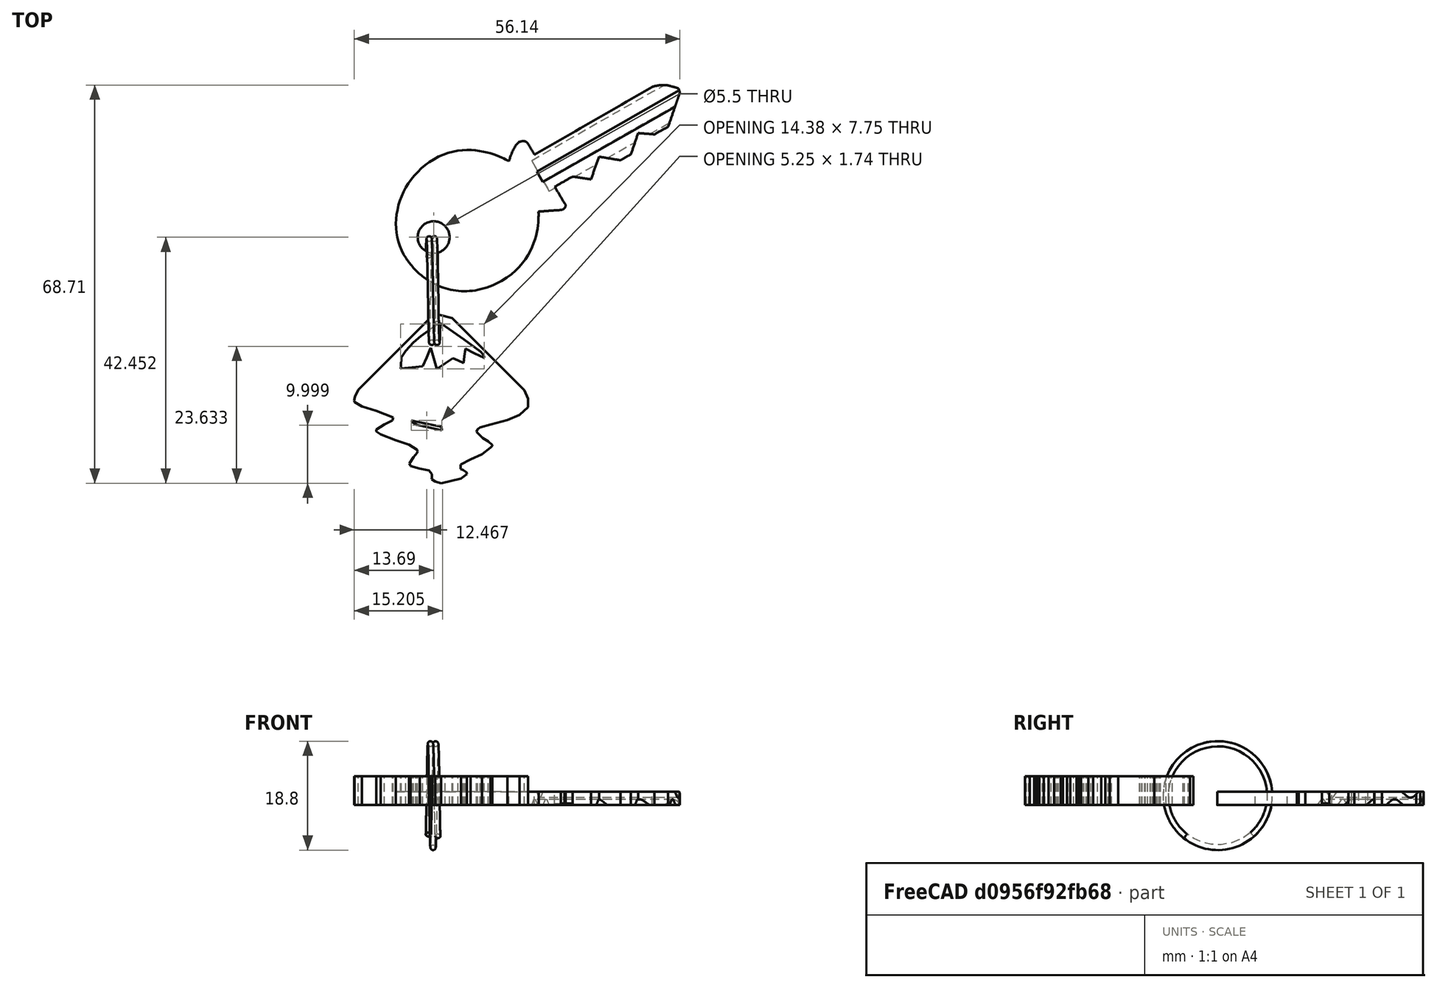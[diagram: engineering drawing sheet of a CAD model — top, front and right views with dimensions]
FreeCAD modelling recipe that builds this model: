
FCSTD DOCUMENT  (FreeCAD 0.16RUnknown)
Label: Inkscape
License: CreativeCommons Attribution-ShareAlike
LicenseURL: http://creativecommons.org/licenses/by-sa/4.0/
objects: Part::Feature×2, Sketcher::SketchObject×1, PartDesign::Pad×1, App::DocumentObjectGroup×1
note: 5 computed .brp shape members not serialized (recipe doc carries the construction recipe); baked Part::Feature solids carry a one-line shape summary decoded from their .brp

FEATURE [Part::Feature] Sweep  label="key-ring-model-1"
  Placement = pos=(-1.2,30.2546,1.6391) rot=(0.333333,0.881918,0.333333;1.69612rad)
  shape: bbox 3.31 x 27.02 x 26.33 mm, 4 faces (baked)
FEATURE [Part::Feature] Cut  label="key-model-1"
  Placement = pos=(-5.46976,36.5266,0) rot=(0,0,1;0.517888rad)
  shape: bbox 49.82 x 36.6 x 2.3 mm, 44 faces (baked)
FEATURE [Sketcher::SketchObject] Sketch
  Placement = pos=(-14,-3,0) rot=(0,0,1;0rad)
  sketch-geometry (100):
    g0: LineSegment StartX=14.9723 StartY=0.01996 StartZ=0 EndX=13.969 EndY=0.29362 EndZ=0
    g1: LineSegment StartX=13.969 StartY=0.29362 StartZ=0 EndX=13.4545 EndY=0.63683 EndZ=0
    g2: LineSegment StartX=13.4545 StartY=0.63683 StartZ=0 EndX=13.3615 EndY=0.71973 EndZ=0
    g3: LineSegment StartX=13.3615 StartY=0.71973 StartZ=0 EndX=13.3914 EndY=0.86552 EndZ=0
    g4: LineSegment StartX=13.3914 StartY=0.86552 StartZ=0 EndX=13.3893 EndY=1.61247 EndZ=0
    g5: LineSegment StartX=13.3893 StartY=1.61247 StartZ=0 EndX=12.8847 EndY=2.22865 EndZ=0
    g6: LineSegment StartX=12.8847 StartY=2.22865 StartZ=0 EndX=11.2899 EndY=2.54694 EndZ=0
    g7: LineSegment StartX=11.2899 StartY=2.54694 StartZ=0 EndX=9.72868 EndY=3.01166 EndZ=0
    g8: LineSegment StartX=9.72868 StartY=3.01166 StartZ=0 EndX=9.53403 EndY=3.44951 EndZ=0
    g9: LineSegment StartX=9.53403 StartY=3.44951 StartZ=0 EndX=10.2264 EndY=4.50306 EndZ=0
    g10: LineSegment StartX=10.2264 StartY=4.50306 StartZ=0 EndX=10.8519 EndY=5.26952 EndZ=0
    g11: LineSegment StartX=10.8519 StartY=5.26952 StartZ=0 EndX=10.9182 EndY=5.55618 EndZ=0
    g12: LineSegment StartX=10.9182 StartY=5.55618 StartZ=0 EndX=10.8647 EndY=5.80745 EndZ=0
    g13: LineSegment StartX=10.8647 StartY=5.80745 StartZ=0 EndX=9.42827 EndY=6.68953 EndZ=0
    g14: LineSegment StartX=9.42827 StartY=6.68953 StartZ=0 EndX=7.16865 EndY=7.4626 EndZ=0
    g15: LineSegment StartX=7.16865 StartY=7.4626 StartZ=0 EndX=4.54116 EndY=8.42539 EndZ=0
    g16: LineSegment StartX=4.54116 StartY=8.42539 StartZ=0 EndX=3.80169 EndY=8.95806 EndZ=0
    g17: LineSegment StartX=3.80169 StartY=8.95806 StartZ=0 EndX=3.82144 EndY=9.29026 EndZ=0
    g18: LineSegment StartX=3.82144 StartY=9.29026 StartZ=0 EndX=5.22954 EndY=10.1505 EndZ=0
    g19: LineSegment StartX=5.22954 StartY=10.1505 StartZ=0 EndX=6.5764 EndY=10.8898 EndZ=0
    g20: LineSegment StartX=6.5764 StartY=10.8898 StartZ=0 EndX=6.7328 EndY=11.3699 EndZ=0
    g21: LineSegment StartX=6.7328 StartY=11.3699 StartZ=0 EndX=3.78128 EndY=12.5284 EndZ=0
    g22: LineSegment StartX=3.78128 StartY=12.5284 StartZ=0 EndX=1.3436 EndY=13.293 EndZ=0
    g23: LineSegment StartX=1.3436 StartY=13.293 StartZ=0 EndX=0.040635 EndY=14.0073 EndZ=0
    g24: LineSegment StartX=0.040635 StartY=14.0073 StartZ=0 EndX=0.011515 EndY=14.3104 EndZ=0
    g25: LineSegment StartX=0.011515 StartY=14.3104 StartZ=0 EndX=0.11094 EndY=14.9231 EndZ=0
    g26: LineSegment StartX=0.11094 StartY=14.9231 StartZ=0 EndX=0.72019 EndY=16.1523 EndZ=0
    g27: LineSegment StartX=0.72019 StartY=16.1523 StartZ=0 EndX=12.7047 EndY=28.1569 EndZ=0
    g28: LineSegment StartX=12.7047 StartY=28.1569 StartZ=0 EndX=14.6713 EndY=29.0574 EndZ=0
    g29: LineSegment StartX=14.6713 StartY=29.0574 StartZ=0 EndX=16.8687 EndY=28.5002 EndZ=0
    g30: LineSegment StartX=16.8687 StartY=28.5002 StartZ=0 EndX=23.1363 EndY=22.3154 EndZ=0
    g31: LineSegment StartX=23.1363 StartY=22.3154 StartZ=0 EndX=29.3179 EndY=16.0918 EndZ=0
    g32: LineSegment StartX=29.3179 StartY=16.0918 StartZ=0 EndX=29.9562 EndY=14.6071 EndZ=0
    g33: LineSegment StartX=29.9562 StartY=14.6071 StartZ=0 EndX=29.9996 EndY=13.8545 EndZ=0
    g34: LineSegment StartX=29.9996 StartY=13.8545 StartZ=0 EndX=29.9574 EndY=13.1752 EndZ=0
    g35: LineSegment StartX=29.9574 StartY=13.1752 StartZ=0 EndX=28.4778 EndY=11.7923 EndZ=0
    g36: LineSegment StartX=28.4778 StartY=11.7923 StartZ=0 EndX=26.3908 EndY=10.9277 EndZ=0
    g37: LineSegment StartX=26.3908 StartY=10.9277 StartZ=0 EndX=23.5813 EndY=10.1632 EndZ=0
    g38: LineSegment StartX=23.5813 StartY=10.1632 StartZ=0 EndX=21.7387 EndY=9.65715 EndZ=0
    g39: LineSegment StartX=21.7387 StartY=9.65715 StartZ=0 EndX=21.2697 EndY=9.3262 EndZ=0
    g40: LineSegment StartX=21.2697 StartY=9.3262 StartZ=0 EndX=21.0559 EndY=8.90651 EndZ=0
    g41: LineSegment StartX=21.0559 StartY=8.90651 StartZ=0 EndX=22.1766 EndY=7.84484 EndZ=0
    g42: LineSegment StartX=22.1766 StartY=7.84484 StartZ=0 EndX=23.1097 EndY=7.23411 EndZ=0
    g43: LineSegment StartX=23.1097 StartY=7.23411 StartZ=0 EndX=23.7835 EndY=6.58282 EndZ=0
    g44: LineSegment StartX=23.7835 StartY=6.58282 StartZ=0 EndX=23.8405 EndY=6.49532 EndZ=0
    g45: LineSegment StartX=23.8405 StartY=6.49532 StartZ=0 EndX=23.5002 EndY=6.16012 EndZ=0
    g46: LineSegment StartX=23.5002 StartY=6.16012 StartZ=0 EndX=22.0161 EndY=5.01097 EndZ=0
    g47: LineSegment StartX=22.0161 StartY=5.01097 StartZ=0 EndX=20.0595 EndY=4.10169 EndZ=0
    g48: LineSegment StartX=20.0595 StartY=4.10169 StartZ=0 EndX=18.378 EndY=3.22979 EndZ=0
    g49: LineSegment StartX=18.378 StartY=3.22979 StartZ=0 EndX=18.3685 EndY=2.50993 EndZ=0
    g50: LineSegment StartX=18.3685 StartY=2.50993 StartZ=0 EndX=18.8154 EndY=2.26555 EndZ=0
    g51: LineSegment StartX=18.8154 StartY=2.26555 StartZ=0 EndX=19.3783 EndY=1.89959 EndZ=0
    g52: LineSegment StartX=19.3783 StartY=1.89959 StartZ=0 EndX=19.4161 EndY=1.59023 EndZ=0
    g53: LineSegment StartX=19.4161 StartY=1.59023 StartZ=0 EndX=18.3915 EndY=0.83028 EndZ=0
    g54: LineSegment StartX=18.3915 StartY=0.83028 StartZ=0 EndX=14.9723 EndY=0.02 EndZ=0
    g55: LineSegment StartX=14.9723 StartY=0.02 StartZ=0 EndX=14.9723 EndY=0.01996 EndZ=0
    g56: LineSegment StartX=15.1028 StartY=9.21545 StartZ=0 EndX=15.0521 EndY=9.78162 EndZ=0
    g57: LineSegment StartX=15.0521 StartY=9.78162 StartZ=0 EndX=15.0423 EndY=9.84262 EndZ=0
    g58: LineSegment StartX=15.0423 StartY=9.84262 StartZ=0 EndX=14.6762 EndY=9.86682 EndZ=0
    g59: LineSegment StartX=14.6762 StartY=9.86682 StartZ=0 EndX=10.5789 EndY=10.7026 EndZ=0
    g60: LineSegment StartX=10.5789 StartY=10.7026 StartZ=0 EndX=9.85139 EndY=10.8875 EndZ=0
    g61: LineSegment StartX=9.85139 StartY=10.8875 StartZ=0 EndX=10.0803 EndY=10.5736 EndZ=0
    g62: LineSegment StartX=10.0803 StartY=10.5736 StartZ=0 EndX=10.7983 EndY=10.0849 EndZ=0
    g63: LineSegment StartX=10.7983 StartY=10.0849 StartZ=0 EndX=14.872 EndY=9.181 EndZ=0
    g64: LineSegment StartX=14.872 StartY=9.181 StartZ=0 EndX=15.0877 EndY=9.1508 EndZ=0
    g65: LineSegment StartX=15.0877 StartY=9.1508 StartZ=0 EndX=15.1028 EndY=9.2154 EndZ=0
    g66: LineSegment StartX=15.1028 StartY=9.2154 StartZ=0 EndX=15.1028 EndY=9.21545 EndZ=0
    g67: LineSegment StartX=15.6546 StartY=20.6875 StartZ=0 EndX=17.0199 EndY=21.5953 EndZ=0
    g68: LineSegment StartX=17.0199 StartY=21.5953 StartZ=0 EndX=17.9329 EndY=21.1895 EndZ=0
    g69: LineSegment StartX=17.9329 StartY=21.1895 StartZ=0 EndX=18.8292 EndY=20.7752 EndZ=0
    g70: LineSegment StartX=18.8292 StartY=20.7752 StartZ=0 EndX=18.9849 EndY=21.9323 EndZ=0
    g71: LineSegment StartX=18.9849 StartY=21.9323 StartZ=0 EndX=19.1478 EndY=23.1581 EndZ=0
    g72: LineSegment StartX=19.1478 StartY=23.1581 StartZ=0 EndX=19.159 EndY=23.2306 EndZ=0
    g73: LineSegment StartX=19.159 StartY=23.2306 StartZ=0 EndX=20.7738 EndY=22.4507 EndZ=0
    g74: LineSegment StartX=20.7738 StartY=22.4507 StartZ=0 EndX=22.4056 EndY=21.6709 EndZ=0
    g75: LineSegment StartX=22.4056 StartY=21.6709 StartZ=0 EndX=22.3565 EndY=21.9987 EndZ=0
    g76: LineSegment StartX=22.3565 StartY=21.9987 StartZ=0 EndX=22.2432 EndY=22.2464 EndZ=0
    g77: LineSegment StartX=22.2432 StartY=22.2464 StartZ=0 EndX=21.7953 EndY=22.7151 EndZ=0
    g78: LineSegment StartX=21.7953 StartY=22.7151 StartZ=0 EndX=18.9166 EndY=24.8482 EndZ=0
    g79: LineSegment StartX=18.9166 StartY=24.8482 StartZ=0 EndX=15.0928 EndY=27.5285 EndZ=0
    g80: LineSegment StartX=15.0928 StartY=27.5285 StartZ=0 EndX=14.6198 EndY=27.5184 EndZ=0
    g81: LineSegment StartX=14.6198 StartY=27.5184 StartZ=0 EndX=14.0994 EndY=27.2608 EndZ=0
    g82: LineSegment StartX=14.0994 StartY=27.2608 StartZ=0 EndX=12.795 EndY=26.334 EndZ=0
    g83: LineSegment StartX=12.795 StartY=26.334 StartZ=0 EndX=11.4628 EndY=25.396 EndZ=0
    g84: LineSegment StartX=11.4628 StartY=25.396 StartZ=0 EndX=10.2049 EndY=24.3415 EndZ=0
    g85: LineSegment StartX=10.2049 StartY=24.3415 StartZ=0 EndX=8.88617 EndY=22.8491 EndZ=0
    g86: LineSegment StartX=8.88617 StartY=22.8491 StartZ=0 EndX=8.11932 EndY=21.701 EndZ=0
    g87: LineSegment StartX=8.11932 StartY=21.701 StartZ=0 EndX=8.03316 EndY=20.1709 EndZ=0
    g88: LineSegment StartX=8.03316 StartY=20.1709 StartZ=0 EndX=8.02454 EndY=19.8448 EndZ=0
    g89: LineSegment StartX=8.02454 StartY=19.8448 StartZ=0 EndX=8.07692 EndY=19.8456 EndZ=0
    g90: LineSegment StartX=8.07692 StartY=19.8456 StartZ=0 EndX=9.9845 EndY=20.0321 EndZ=0
    g91: LineSegment StartX=9.9845 StartY=20.0321 StartZ=0 EndX=11.8397 EndY=20.2176 EndZ=0
    g92: LineSegment StartX=11.8397 StartY=20.2176 StartZ=0 EndX=12.4871 EndY=21.7319 EndZ=0
    g93: LineSegment StartX=12.4871 StartY=21.7319 StartZ=0 EndX=13.1663 EndY=23.324 EndZ=0
    g94: LineSegment StartX=13.1663 StartY=23.324 StartZ=0 EndX=13.2055 EndY=23.3942 EndZ=0
    g95: LineSegment StartX=13.2055 StartY=23.3942 StartZ=0 EndX=13.7275 EndY=21.6107 EndZ=0
    g96: LineSegment StartX=13.7275 StartY=21.6107 StartZ=0 EndX=14.2524 EndY=19.7993 EndZ=0
    g97: LineSegment StartX=14.2524 StartY=19.7993 StartZ=0 EndX=14.2865 EndY=19.778 EndZ=0
    g98: LineSegment StartX=14.2865 StartY=19.778 StartZ=0 EndX=15.6546 EndY=20.6876 EndZ=0
    g99: LineSegment StartX=15.6546 StartY=20.6876 StartZ=0 EndX=15.6546 EndY=20.6875 EndZ=0
  constraints (56):
    c: Coincident(g0,g1)
    c: Coincident(g1,g2)
    c: Coincident(g2,g3)
    c: Coincident(g3,g4)
    c: Coincident(g4,g5)
    c: Coincident(g5,g6)
    c: Coincident(g6,g7)
    c: Coincident(g7,g8)
    c: Coincident(g8,g9)
    c: Coincident(g9,g10)
    c: Coincident(g10,g11)
    c: Coincident(g11,g12)
    c: Coincident(g12,g13)
    c: Coincident(g13,g14)
    c: Coincident(g14,g15)
    c: Coincident(g15,g16)
    c: Coincident(g16,g17)
    c: Coincident(g17,g18)
    c: Coincident(g18,g19)
    c: Coincident(g19,g20)
    c: Coincident(g20,g21)
    c: Coincident(g21,g22)
    c: Coincident(g22,g23)
    c: Coincident(g23,g24)
    c: Coincident(g24,g25)
    c: Coincident(g25,g26)
    c: Coincident(g26,g27)
    c: Coincident(g27,g28)
    c: Coincident(g28,g29)
    c: Coincident(g29,g30)
    c: Coincident(g30,g31)
    c: Coincident(g31,g32)
    c: Coincident(g32,g33)
    c: Coincident(g33,g34)
    c: Coincident(g34,g35)
    c: Coincident(g35,g36)
    c: Coincident(g36,g37)
    c: Coincident(g37,g38)
    c: Coincident(g38,g39)
    c: Coincident(g39,g40)
    c: Coincident(g40,g41)
    c: Coincident(g41,g42)
    c: Coincident(g42,g43)
    c: Coincident(g43,g44)
    c: Coincident(g44,g45)
    c: Coincident(g45,g46)
    c: Coincident(g46,g47)
    c: Coincident(g47,g48)
    c: Coincident(g48,g49)
    c: Coincident(g49,g50)
    c: Coincident(g50,g51)
    c: Coincident(g51,g52)
    c: Coincident(g52,g53)
    c: Coincident(g53,g54)
    c: Coincident(g54,g55)
    c: Coincident(g55,g0)
FEATURE [PartDesign::Pad] Pad
  Length = 5
  Length2 = 100
  Placement = pos=(-14,-3,0) rot=(0,0,1;0rad)
  Sketch = -> Sketch
  Type = 0
FEATURE [App::DocumentObjectGroup] Group  label="Assembly"
  Group = -> [Sweep,Cut,Pad]
